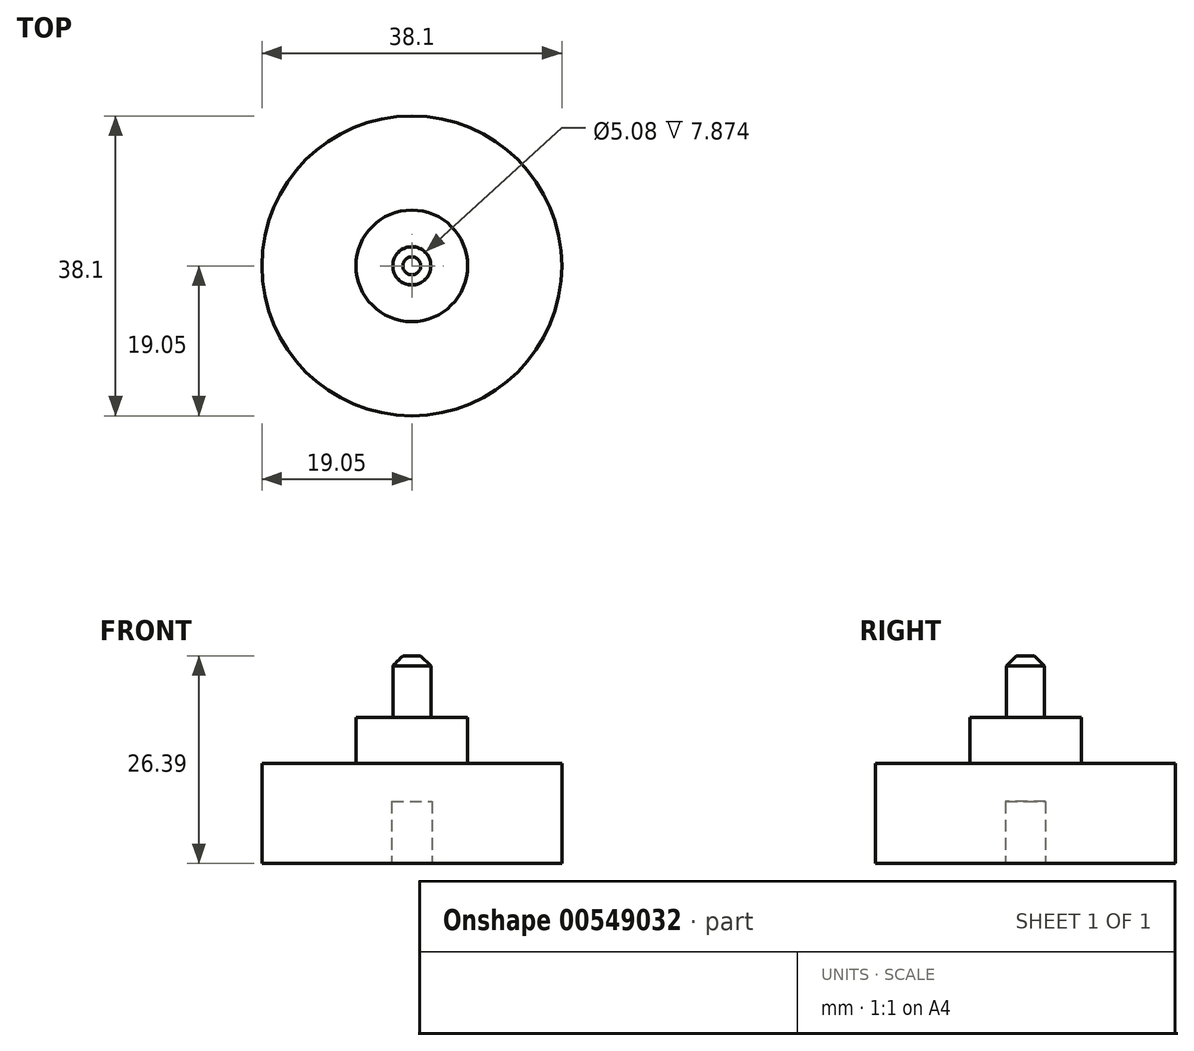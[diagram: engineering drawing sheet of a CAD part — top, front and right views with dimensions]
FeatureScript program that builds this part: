
annotation { "Feature Type Name" : "Feature", "Feature Type Description" : "" }
export const myFeature = defineFeature(function(context is Context, id is Id, definition is map)
    precondition{}
    {
        {
            var Q0;
            Q0=qCreatedBy(makeId("Front.planeOp"),FACE);
            var sketch = newSketch(context, id + "F0", { "sketchPlane" : qUnion([Q0])});
            skLineSegment(sketch, "E0", {"start": v(19.05, 0) * mm, "end": v(19.05, 12.7) * mm});
            skLineSegment(sketch, "E1", {"start": v(19.05, 12.7) * mm, "end": v(7.09, 12.7) * mm});
            skLineSegment(sketch, "E2", {"start": v(2.41, 18.54) * mm, "end": v(7.09, 18.54) * mm});
            skLineSegment(sketch, "E3", {"start": v(7.09, 18.54) * mm, "end": v(7.09, 12.7) * mm});
            skLineSegment(sketch, "E4", {"start": v(0, 26.4) * mm, "end": v(2.41, 26.4) * mm});
            skLineSegment(sketch, "E5", {"start": v(2.41, 26.4) * mm, "end": v(2.41, 18.54) * mm});
            skPoint(sketch, "E6.start.orphan", {"position": v(0, 12.7) * mm});
            skPoint(sketch, "E7.start.orphan", {"position": v(0, 18.54) * mm});
            skLineSegment(sketch, "E8", {"start": v(2.54, 0) * mm, "end": v(2.54, 7.87) * mm});
            skLineSegment(sketch, "E9", {"start": v(2.54, 7.87) * mm, "end": v(0, 7.87) * mm});
            skLineSegment(sketch, "E10", {"start": v(0, 7.87) * mm, "end": v(0, 26.4) * mm});
            skLineSegment(sketch, "E11", {"start": v(2.54, 0) * mm, "end": v(19.05, 0) * mm});
            skSolve(sketch);
        }
        {
            var Q0;
            Q0 = qSketchRegion(id + "F0", true);
            var Q1;
            Q1=sQuery(id+"F0.wireOp",EDGE,"E10");
            revolve(context, id + "F1", {"entities" : qUnion([Q0]), "axis" : qUnion([Q1]), "revolveType" : RevolveType.FULL});
        }
        {
            var Q0;
            Q0=makeQuery(id+"F1.opRevolve","SWEPT_EDGE",EDGE,{"disambiguationData":[OSD([sQuery(id+"F0.wireOp",EDGE,"E4"),sQuery(id+"F0.wireOp",EDGE,"E5")])]});
            chamfer(context, id + "F2", {"entities" : qUnion([Q0]), "width" : 1.27 * mm, "tangentPropagation" : true});
        }
    });
